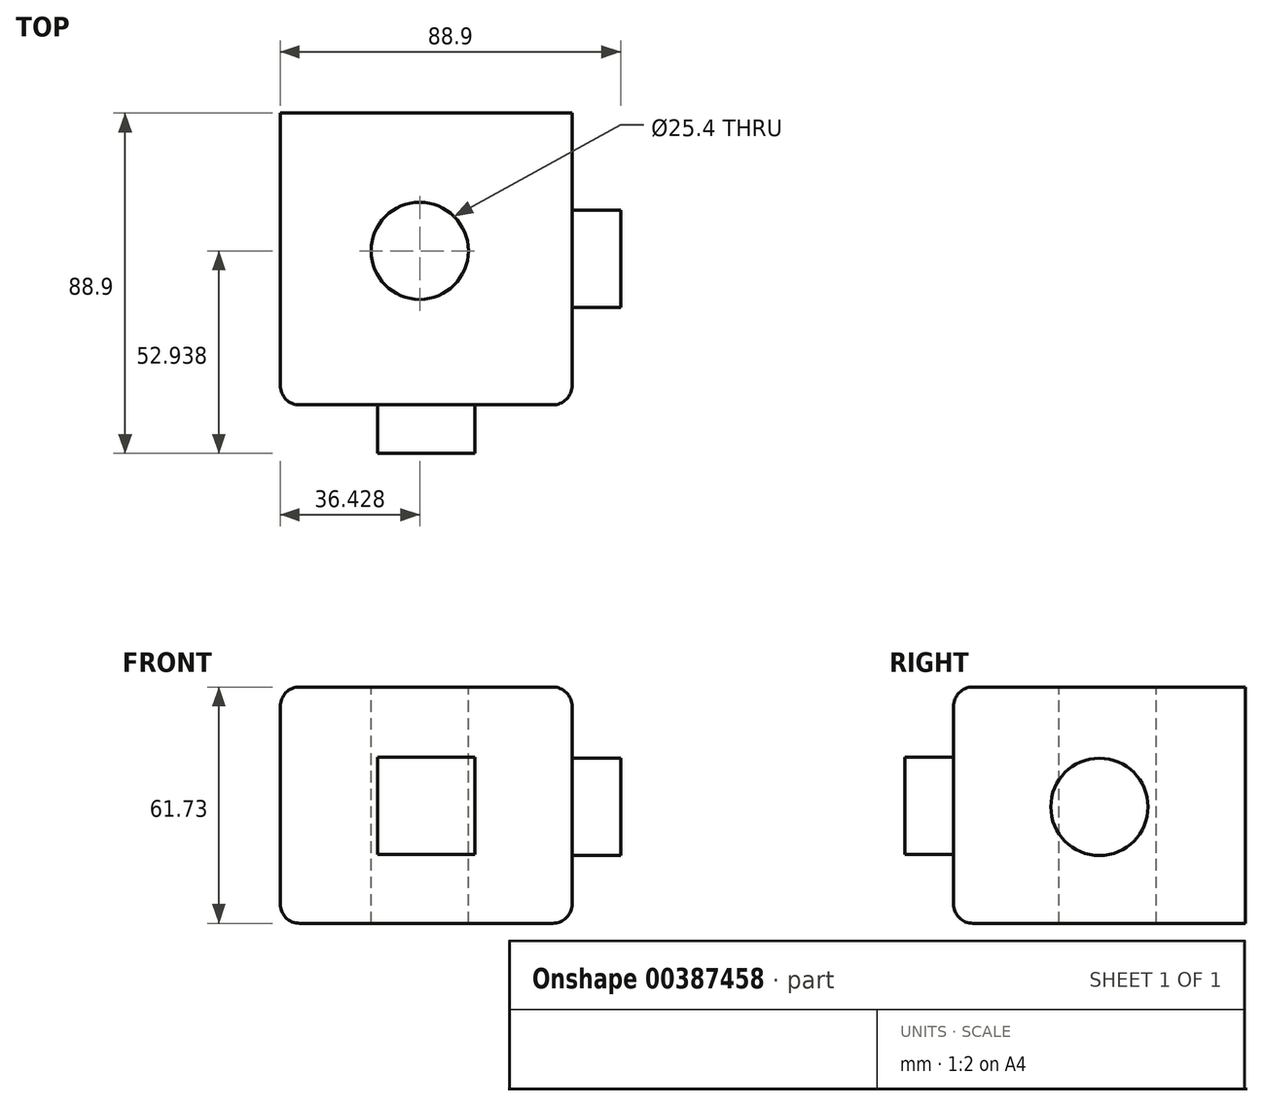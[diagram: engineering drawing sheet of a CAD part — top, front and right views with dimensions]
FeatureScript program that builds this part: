
annotation { "Feature Type Name" : "Feature", "Feature Type Description" : "" }
export const myFeature = defineFeature(function(context is Context, id is Id, definition is map)
    precondition{}
    {
        {
            var Q0;
            Q0=qCreatedBy(makeId("Front.planeOp"),FACE);
            var sketch = newSketch(context, id + "F0", { "sketchPlane" : qUnion([Q0])});
            skLineSegment(sketch, "E0.bottom", {"start": v(0, 0) * mm, "end": v(76.2, 0) * mm});
            skLineSegment(sketch, "E0.top", {"start": v(0, 61.73) * mm, "end": v(76.2, 61.73) * mm});
            skLineSegment(sketch, "E0.left", {"start": v(0, 0) * mm, "end": v(0, 61.73) * mm});
            skLineSegment(sketch, "E0.right", {"start": v(76.2, 0) * mm, "end": v(76.2, 61.73) * mm});
            skSolve(sketch);
        }
        {
            var Q0;
            Q0=makeQuery(id+"F0.imprint","IMPRINT",FACE,{"disambiguationData":[TD([[makeQuery(id+"F0.imprint","IMPRINT",EDGE,{"derivedFrom":sQuery(id+"F0.wireOp",EDGE,"E0.bottom")}),1.0]])]});
            extrude(context, id + "F1", {"entities" : qUnion([Q0]), "depth" : 76.2 * mm});
        }
        {
            var Q0;
            Q0=makeQuery(id+"F1.opExtrude","SWEPT_FACE",FACE,{"disambiguationData":[OSD([sQuery(id+"F0.wireOp",EDGE,"E0.top")])]});
            var sketch = newSketch(context, id + "F2", { "sketchPlane" : qUnion([Q0])});
            skPoint(sketch, "E1", {"position": v(39.27, -38.1) * mm});
            skPoint(sketch, "E1.positionSnap0", {"position": v(76.2, -38.1) * mm});
            skSolve(sketch);
        }
        {
            var Q0;
            {var subQ0=sQuery(id+"F0.wireOp",EDGE,"E0.top");Q0=makeQuery(id+"F2.imprint","IMPRINT",FACE,{"disambiguationData":[TD([[makeQuery(id+"F2.imprint","IMPRINT",EDGE,{"derivedFrom":makeQuery(id+"F1.opExtrude","CAP_EDGE",EDGE,{"disambiguationData":[OSD([subQ0])],"isStart":true})}),-1.0]])]});}
            var sketch = newSketch(context, id + "F3", { "sketchPlane" : qUnion([Q0])});
            skSolve(sketch);
        }
        {
            var Q0;
            Q0=makeQuery(id+"F1.opExtrude","SWEPT_FACE",FACE,{"disambiguationData":[OSD([sQuery(id+"F0.wireOp",EDGE,"E0.right")])]});
            var sketch = newSketch(context, id + "F4", { "sketchPlane" : qUnion([Q0])});
            skCircle(sketch, "E2", {"center": v(-38.1, 30.43) * mm, "radius": 12.7 * mm});
            skPoint(sketch, "E2.centerSnap0", {"position": v(-38.1, 61.73) * mm});
            skSolve(sketch);
        }
        {
            var Q0;
            Q0=makeQuery(id+"F4.imprint","IMPRINT",FACE,{"disambiguationData":[TD([[makeQuery(id+"F4.imprint","IMPRINT",EDGE,{"derivedFrom":sQuery(id+"F4.wireOp",EDGE,"E2")}),1.0]])]});
            extrude(context, id + "F5", {"entities" : qUnion([Q0]), "operationType" : NewBodyOperationType.ADD, "depth" : 12.7 * mm});
        }
        {
            var Q0;
            Q0=makeQuery(id+"F1.opExtrude","CAP_FACE",FACE,{"disambiguationData":[OSD([sQuery(id+"F0.wireOp",EDGE,"E0.bottom"),sQuery(id+"F0.wireOp",EDGE,"E0.top"),sQuery(id+"F0.wireOp",EDGE,"E0.left"),sQuery(id+"F0.wireOp",EDGE,"E0.right")])],"isStart":false});
            var sketch = newSketch(context, id + "F6", { "sketchPlane" : qUnion([Q0])});
            skSolve(sketch);
        }
        {
            var Q0;
            Q0=makeQuery(id+"F6.imprint","IMPRINT",FACE,{"disambiguationData":[TD([[makeQuery(id+"F6.imprint","IMPRINT",EDGE,{"derivedFrom":makeQuery(id+"F1.opExtrude","CAP_EDGE",EDGE,{"disambiguationData":[OSD([sQuery(id+"F0.wireOp",EDGE,"E0.bottom")])],"isStart":false})}),1.0]])]});
            var sketch = newSketch(context, id + "F7", { "sketchPlane" : qUnion([Q0])});
            skLineSegment(sketch, "E3.bottom", {"start": v(25.4, 18.05) * mm, "end": v(50.8, 18.05) * mm});
            skLineSegment(sketch, "E3.top", {"start": v(25.4, 43.45) * mm, "end": v(50.8, 43.45) * mm});
            skLineSegment(sketch, "E3.left", {"start": v(25.4, 18.05) * mm, "end": v(25.4, 43.45) * mm});
            skLineSegment(sketch, "E3.right", {"start": v(50.8, 18.05) * mm, "end": v(50.8, 43.45) * mm});
            skSolve(sketch);
        }
        {
            var Q0;
            Q0=makeQuery(id+"F7.imprint","IMPRINT",FACE,{"disambiguationData":[TD([[makeQuery(id+"F7.imprint","IMPRINT",EDGE,{"derivedFrom":sQuery(id+"F7.wireOp",EDGE,"E3.bottom")}),1.0]])]});
            extrude(context, id + "F8", {"entities" : qUnion([Q0]), "operationType" : NewBodyOperationType.ADD, "depth" : 12.7 * mm});
        }
        {
            var Q0;
            {var subQ0=sQuery(id+"F0.wireOp",EDGE,"E0.top");Q0=makeQuery(id+"F3.imprint","IMPRINT",FACE,{"disambiguationData":[TD([[makeQuery(id+"F3.imprint","IMPRINT",EDGE,{"derivedFrom":makeQuery(id+"F2.imprint","IMPRINT",EDGE,{"derivedFrom":makeQuery(id+"F1.opExtrude","CAP_EDGE",EDGE,{"disambiguationData":[OSD([subQ0])],"isStart":true})})}),-1.0]])]});}
            var sketch = newSketch(context, id + "F9", { "sketchPlane" : qUnion([Q0])});
            skCircle(sketch, "E4", {"center": v(36.43, -35.96) * mm, "radius": 12.7 * mm});
            skSolve(sketch);
        }
        {
            var Q0;
            Q0=sQuery(id+"F9.wireOp",VERTEX,"E4.center");
            var Q1;
            Q1=makeQuery(id+"F1.opExtrude","SWEPT_BODY",BODY,{"disambiguationData":[OSD([sQuery(id+"F0.wireOp",EDGE,"E0.bottom"),sQuery(id+"F0.wireOp",EDGE,"E0.top"),sQuery(id+"F0.wireOp",EDGE,"E0.left"),sQuery(id+"F0.wireOp",EDGE,"E0.right")])]});
            hole(context, id + "F10", {"style" : HoleStyle.SIMPLE, "endStyle" : HoleEndStyle.THROUGH, "holeDiameter" : 25.4 * mm, "isTappedThrough" : true, "tappedDepth" : 12.7 * mm, "tapClearance" : 3, "locations" : qUnion([Q0]), "scope" : qUnion([Q1])});
        }
        {
            var Q0;
            Q0=makeQuery(id+"F1.opExtrude","CAP_EDGE",EDGE,{"disambiguationData":[OSD([sQuery(id+"F0.wireOp",EDGE,"E0.top")])],"isStart":false});
            fillet(context, id + "F11", {"entities" : qUnion([Q0]), "radius" : 5.08 * mm, "tangentPropagation" : true, "allowEdgeOverflow" : false});
        }
        {
            var Q0;
            Q0=makeQuery(id+"F1.opExtrude","SWEPT_EDGE",EDGE,{"disambiguationData":[OSD([sQuery(id+"F0.wireOp",EDGE,"E0.top"),sQuery(id+"F0.wireOp",EDGE,"E0.right")])]});
            fillet(context, id + "F12", {"entities" : qUnion([Q0]), "radius" : 5.08 * mm, "tangentPropagation" : true, "allowEdgeOverflow" : false});
        }
        {
            var Q0;
            Q0=makeQuery(id+"F1.opExtrude","SWEPT_EDGE",EDGE,{"disambiguationData":[OSD([sQuery(id+"F0.wireOp",EDGE,"E0.top"),sQuery(id+"F0.wireOp",EDGE,"E0.left")])]});
            fillet(context, id + "F13", {"entities" : qUnion([Q0]), "radius" : 5.08 * mm, "tangentPropagation" : true, "allowEdgeOverflow" : false});
        }
        {
            var Q0;
            Q0=makeQuery(id+"F1.opExtrude","CAP_EDGE",EDGE,{"disambiguationData":[OSD([sQuery(id+"F0.wireOp",EDGE,"E0.bottom")])],"isStart":false});
            fillet(context, id + "F14", {"entities" : qUnion([Q0]), "radius" : 5.08 * mm, "tangentPropagation" : true, "allowEdgeOverflow" : false});
        }
    });
